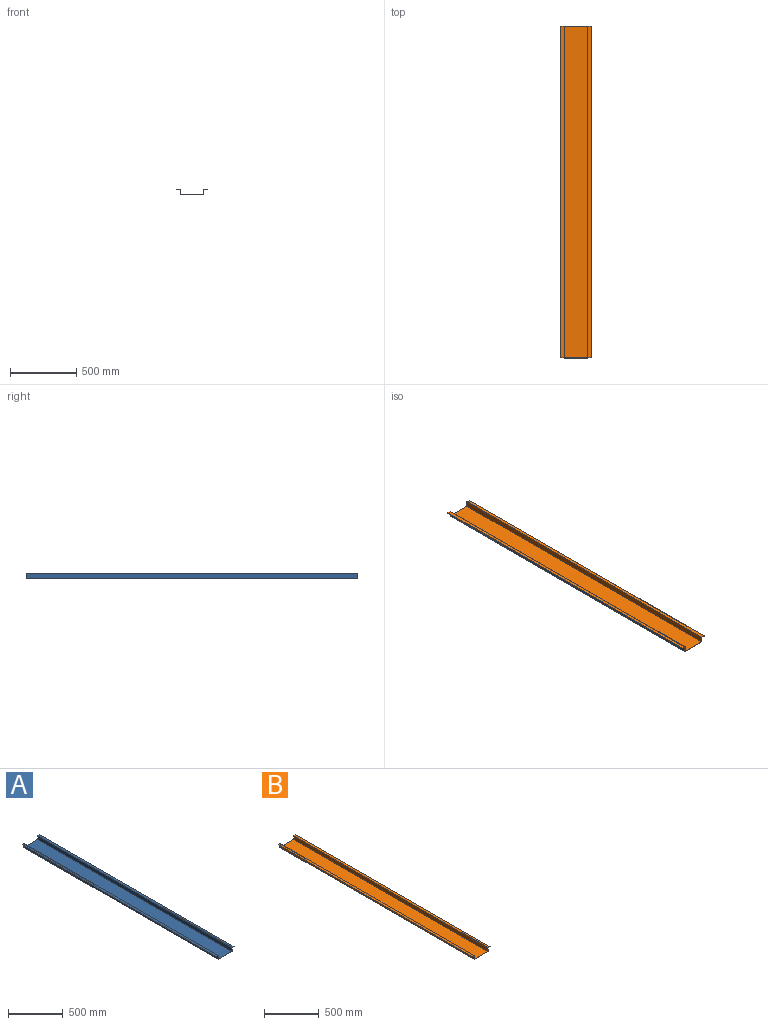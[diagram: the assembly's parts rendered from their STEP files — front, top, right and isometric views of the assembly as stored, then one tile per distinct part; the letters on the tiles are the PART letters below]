
ASSEMBLY  parts=2 mates=1
PART A: 18 faces, bbox 230.8x2500x41.4 mm
  f0: plane 2500x24.8mm, normal (0,0,1), area 61987.7mm2, adj f1,f15,f16,f17
  f1: cylinder r=0.35mm len=2500mm, axis (0,1,0), area 2748.9mm2, adj f0,f2,f16,f17
  f2: plane 2500x0.7mm, normal (0,0,1), area 1750mm2, adj f1,f3,f16,f17
  f3: plane 2500x40mm, normal (-1,0,0), area 100000mm2, adj f2,f4,f16,f17
  f4: plane 2500x178.6mm, normal (0,0,1), area 446500mm2, adj f3,f5,f16,f17
  f5: plane 2500x40mm, normal (1,0,0), area 100000mm2, adj f4,f6,f16,f17
  f6: plane 2500x0.7mm, normal (0,0,1), area 1750mm2, adj f5,f7,f16,f17
  f7: cylinder r=0.35mm len=2500mm, axis (0,1,0), area 2748.9mm2, adj f6,f8,f16,f17
  f8: plane 2500x24.8mm, normal (0,0,1), area 61987.7mm2, adj f7,f9,f16,f17
  f9: cylinder r=0.7mm len=2500mm, axis (0,1,0), area 5269.3mm2, adj f8,f10,f16,f17
  f10: plane 2500x24.69mm, normal (0,0,-1), area 61730.4mm2, adj f9,f11,f16,f17
  f11: plane 2500x40mm, normal (-1,0,0), area 100000mm2, adj f10,f12,f16,f17
  f12: plane 2500x180mm, normal (0,0,-1), area 450000mm2, adj f11,f13,f16,f17
  f13: plane 2500x40mm, normal (1,0,0), area 100000mm2, adj f12,f14,f16,f17
  f14: plane 2500x24.69mm, normal (0,0,-1), area 61730.4mm2, adj f13,f15,f16,f17
  f15: cylinder r=0.7mm len=2500mm, axis (0,1,0), area 5269.3mm2, adj f0,f14,f16,f17
  f16: plane 230.79x41.4mm, normal (0,-1,0), area 253.1mm2, adj f0,f1,f2,f3,f4,f5,f6,f7
  f17: plane 230.79x41.4mm, normal (0,1,0), area 253.1mm2, adj f0,f1,f2,f3,f4,f5,f6,f7
PART B: 18 faces, bbox 228.8x2500x41.4 mm
  f0: plane 2500x24.8mm, normal (0,0,1), area 61987.7mm2, adj f1,f15,f16,f17
  f1: cylinder r=0.35mm len=2500mm, axis (0,1,0), area 2748.9mm2, adj f0,f2,f16,f17
  f2: plane 2500x0.7mm, normal (0,0,1), area 1750mm2, adj f1,f3,f16,f17
  f3: plane 2500x40mm, normal (-1,0,0), area 100000mm2, adj f2,f4,f16,f17
  f4: plane 2500x176.6mm, normal (0,0,1), area 441500mm2, adj f3,f5,f16,f17
  f5: plane 2500x40mm, normal (1,0,0), area 100000mm2, adj f4,f6,f16,f17
  f6: plane 2500x0.7mm, normal (0,0,1), area 1750mm2, adj f5,f7,f16,f17
  f7: cylinder r=0.35mm len=2500mm, axis (0,1,0), area 2748.9mm2, adj f6,f8,f16,f17
  f8: plane 2500x24.8mm, normal (0,0,1), area 61987.7mm2, adj f7,f9,f16,f17
  f9: cylinder r=0.7mm len=2500mm, axis (0,1,0), area 5269.3mm2, adj f8,f10,f16,f17
  f10: plane 2500x24.69mm, normal (0,0,-1), area 61730.4mm2, adj f9,f11,f16,f17
  f11: plane 2500x40mm, normal (-1,0,0), area 100000mm2, adj f10,f12,f16,f17
  f12: plane 2500x178mm, normal (0,0,-1), area 445000mm2, adj f11,f13,f16,f17
  f13: plane 2500x40mm, normal (1,0,0), area 100000mm2, adj f12,f14,f16,f17
  f14: plane 2500x24.69mm, normal (0,0,-1), area 61730.4mm2, adj f13,f15,f16,f17
  f15: cylinder r=0.7mm len=2500mm, axis (0,1,0), area 5269.3mm2, adj f0,f14,f16,f17
  f16: plane 228.79x41.4mm, normal (0,-1,0), area 251.7mm2, adj f0,f1,f2,f3,f4,f5,f6,f7
  f17: plane 228.79x41.4mm, normal (0,1,0), area 251.7mm2, adj f0,f1,f2,f3,f4,f5,f6,f7
PLACE A t=(-12.16,1254.1,-257.76)mm fixed
PLACE B t=(-12.16,1254.1,-257.06)mm
MATE fastened B.f12 <-> A.f4  axis (0,0,-1) through (-12.16,1254.1,-257.06)mm
